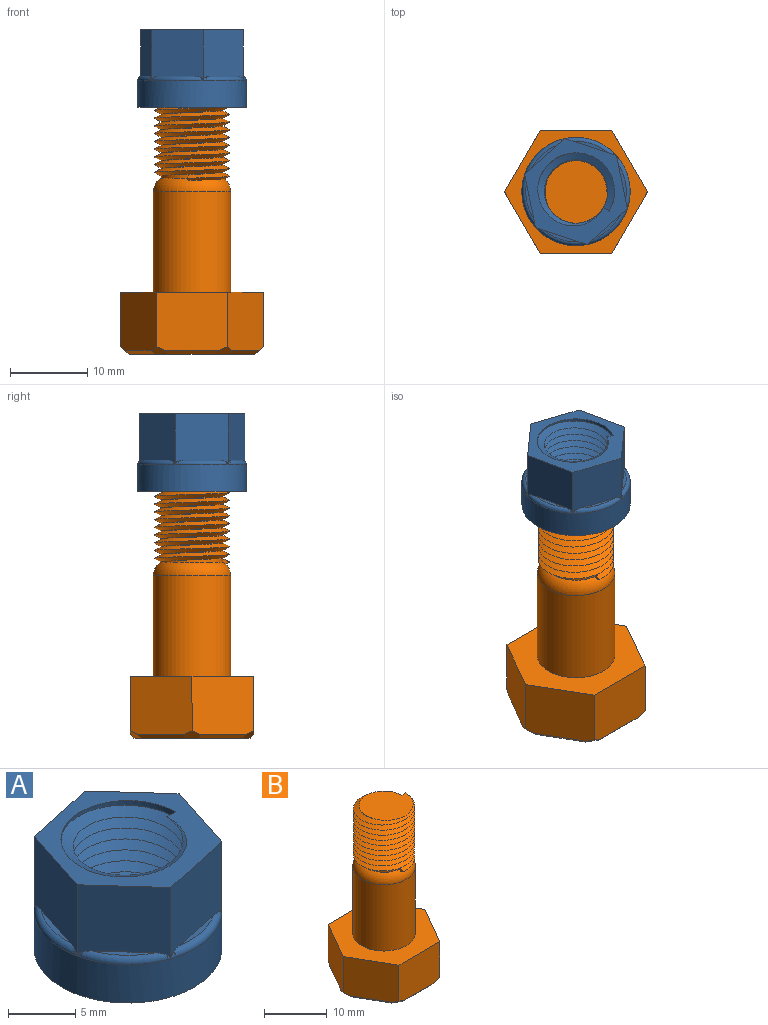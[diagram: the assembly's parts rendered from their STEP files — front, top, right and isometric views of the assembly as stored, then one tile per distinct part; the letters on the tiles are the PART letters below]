
ASSEMBLY  parts=2 mates=1
PART A: 26 faces, bbox 15.8x15.8x11.6 mm
  f0: plane 0.9x0.45mm, normal (0,1,0), area 0.2mm2, adj f8,f9,f25
  f1: bspline ~11.55x10.45mm, area 280.6mm2, adj f8,f9,f24,f25
  f2: plane 7.17x6.82mm, normal (0.21,-0.98,0), area 42.2mm2, adj f3,f7,f9,f22,f23
  f3: plane 6.82x5.52mm, normal (-0.74,-0.67,0), area 42.2mm2, adj f2,f4,f9,f20,f21
  f4: plane 6.99x6.82mm, normal (-0.95,0.31,0), area 42.2mm2, adj f3,f5,f9,f18,f19
  f5: plane 7.17x6.82mm, normal (-0.21,0.98,0), area 42.2mm2, adj f4,f6,f9,f16,f17
  f6: plane 6.82x5.52mm, normal (0.74,0.67,0), area 42.2mm2, adj f5,f7,f9,f14,f15
  f7: plane 6.99x6.82mm, normal (0.95,-0.31,0), area 42.2mm2, adj f2,f6,f9,f11,f12
  f8: cylinder r=5mm len=10mm, axis (0,0,-1), area 59.9mm2, adj f0,f1,f9,f10,f24,f25
  f9: plane 14.37x14.01mm, normal (0,0,1), area 54.8mm2, adj f0,f1,f2,f3,f4,f5,f6,f7
  f10: plane 14.69x14.69mm, normal (0,0,-1), area 81.4mm2, adj f8,f13,f24,f25
  f11: torus R=6.5mm, axis (0,0,1), area 4.8mm2, adj f7,f12,f13
  f12: plane 4.46x1.45mm, normal (0,0,1), area 1.4mm2, adj f7,f11
  f13: cylinder r=7mm len=14mm, axis (0,0,-1), area 153.9mm2, adj f10,f11,f14,f16,f19,f20,f22
  f14: torus R=6.5mm, axis (0,0,1), area 4.8mm2, adj f6,f13,f15
  f15: plane 3.48x3.15mm, normal (0,0,1), area 1.4mm2, adj f6,f14
  f16: torus R=6.5mm, axis (0,0,1), area 4.8mm2, adj f5,f13,f17
  f17: plane 4.59x1.06mm, normal (0,0,1), area 1.4mm2, adj f5,f16
  f18: plane 4.46x1.45mm, normal (0,0,1), area 1.4mm2, adj f4,f19
  f19: torus R=6.5mm, axis (0,0,1), area 4.8mm2, adj f4,f13,f18
  f20: torus R=6.5mm, axis (0,0,1), area 4.8mm2, adj f3,f13,f21
  f21: plane 3.48x3.15mm, normal (0,0,1), area 1.4mm2, adj f3,f20
  f22: torus R=6.5mm, axis (0,0,1), area 4.8mm2, adj f2,f13,f23
  f23: plane 4.59x1.06mm, normal (0,0,1), area 1.4mm2, adj f2,f22
  f24: plane 0.9x0.45mm, normal (0,-1,0), area 0.2mm2, adj f1,f8,f10
  f25: bspline ~11.55x10.45mm, area 281.2mm2, adj f0,f1,f8,f10
PART B: 28 faces, bbox 19.1x16.6x34.1 mm
  f0: cylinder r=4mm len=10.27mm, axis (0,0,-1), area 10.8mm2, adj f1,f23,f24,f25,f26,f27
  f1: torus R=3mm, axis (0,0,1), area 58.6mm2, adj f0,f2,f25,f26
  f2: cylinder r=5mm len=13mm, axis (0,0,-1), area 408.4mm2, adj f1,f9
  f3: plane 9.24x7.5mm, normal (0,-1,0), area 68.8mm2, adj f4,f8,f9,f14,f21,f22
  f4: plane 8x7.5mm, normal (0.87,-0.5,0), area 68.8mm2, adj f3,f5,f9,f16,f17,f21
  f5: plane 8x7.5mm, normal (0.87,0.5,0), area 68.8mm2, adj f4,f6,f9,f15,f17,f18
  f6: plane 9.24x7.5mm, normal (0,1,0), area 68.8mm2, adj f5,f7,f9,f13,f18,f19
  f7: plane 8x7.5mm, normal (-0.87,0.5,0), area 68.8mm2, adj f6,f8,f9,f11,f19,f20
  f8: plane 8x7.5mm, normal (-0.87,-0.5,0), area 68.8mm2, adj f3,f7,f9,f12,f20,f22
  f9: plane 18.48x16mm, normal (0,0,1), area 143.2mm2, adj f2,f3,f4,f5,f6,f7,f8
  f10: plane 16.24x15mm, normal (0,0,-1), area 191.8mm2, adj f11,f12,f13,f14,f15,f16,f17,f18
  f11: plane 6.13x3.83mm, normal (-0.61,0.35,-0.71), area 4.8mm2, adj f7,f10,f19,f20
  f12: plane 6.13x3.83mm, normal (-0.61,-0.35,-0.71), area 4.8mm2, adj f8,f10,f20,f22
  f13: plane 7.08x0.5mm, normal (0,0.71,-0.71), area 4.8mm2, adj f6,f10,f18,f19
  f14: plane 7.08x0.5mm, normal (0,-0.71,-0.71), area 4.8mm2, adj f3,f10,f21,f22
  f15: plane 6.13x3.83mm, normal (0.61,0.35,-0.71), area 4.8mm2, adj f5,f10,f17,f18
  f16: plane 6.13x3.83mm, normal (0.61,-0.35,-0.71), area 4.8mm2, adj f4,f10,f17,f21
  f17: plane 1.87x1.12mm, normal (0.65,0,-0.76), area 2.1mm2, adj f4,f5,f10,f15,f16
  f18: plane 1.91x1.44mm, normal (0.33,0.57,-0.76), area 2.1mm2, adj f5,f6,f10,f13,f15
  f19: plane 1.91x1.44mm, normal (-0.33,0.57,-0.76), area 2.1mm2, adj f6,f7,f10,f11,f13
  f20: plane 1.87x1.12mm, normal (-0.65,0,-0.76), area 2.1mm2, adj f7,f8,f10,f11,f12
  f21: plane 1.91x1.44mm, normal (0.33,-0.57,-0.76), area 2.1mm2, adj f3,f4,f10,f14,f16
  f22: plane 1.91x1.44mm, normal (-0.33,-0.57,-0.76), area 2.1mm2, adj f3,f8,f10,f12,f14
  f23: plane 0.9x0.45mm, normal (0,1,0), area 0.2mm2, adj f0,f26,f27
  f24: bspline ~11.32x10.78mm, area 283.5mm2, adj f0,f25,f26,f27
  f25: plane 0.9x0.72mm, normal (-0.99,0.11,0), area 0.3mm2, adj f0,f1,f24,f26
  f26: bspline ~10.72x9.8mm, area 287.7mm2, adj f0,f1,f23,f24,f25
  f27: plane 9.52x9.03mm, normal (0,0,1), area 55.7mm2, adj f0,f23,f24
PLACE A rot(axis=(0,0,-1),30.3deg) t=(0,0,31.92)mm
PLACE B at identity
MATE cylindrical A.f8 <-> B.f0  axis (0,0,1) through (0,0,41.92)mm
